# Revit family: Columns_&_Screens-Teknion-RCSLG_Lateral_Screen_for_Spine_Desk_Glass-R2019
name_source: partatom
category: Furniture
units: mm (PartAtom-declared; Revit-internal decimal feet)

## family parameters
Always vertical = Yes
Cut with Voids When Loaded = No
OmniClass Number = 23.40.20.00
OmniClass Title = General Furniture and Specialties
Room Calculation Point = No
Shared = Yes
Work Plane-Based = No

## types (9) — shared parameters
Assembly Code = E2020200
Bottom of Screen = 29 "
Manufacturer = Teknion
Manufacturer Fax = 416.661.4586
Part Number = RCSLG
Product Documentation Link = https://www.teknion.com
Product Line = Expansion Desking
Product Page URL = https://www.teknion.com
Series = Expansion Desking
Sustainability Data = https://www.teknion.com
URL = www.teknion.com
Unit Weight URL = http://www.teknion.com
Warranty = http://www.teknion.com

## per-type parameters (varying)
| type | Description | From Rear Edge | From Two Central Screens | From Two Mounted Storage | Height | Model | Screen Offset |
| From Two Central Screens, 51" High Datum Line With Desk-Mounted Option | Lateral Screen for Spine Desk - Glass, From Two Central Screens, 51" High Datum Line with Desk-Mounted option | No | Yes | No | 50.831 " | RCSLGC22__ | 0.508 " |
| From Two Central Screens, 42" High Datum Line With Desk-Mounted Option | Lateral Screen for Spine Desk - Glass, From Two Central Screens, 42" High Datum Line with Desk-Mounted option | No | Yes | No | 42 " | RCSLGC13__ | 0.508 " |
| From Two Central Screens, Desk-Mounted Shelf Height With Desk-Mounted Option | Lateral Screen for Spine Desk - Glass, From Two Central Screens, Desk-Mounted Shelf Height with Desk-Mounted option | No | Yes | No | 36.071 " | RCSLGC07__ | 0.508 " |
| From Rear Edge, 42" High Datum Line With Desk-Mounted Option | Lateral Screen for Spine Desk - Glass, From Rear Edge , 42" High Datum Line with Desk-Mounted option | Yes | No | No | 42 " | RCSLGE13__ | 0 " |
| From Two Mounted Storage, 42" High Datum Line With Desk-Mounted Option | Lateral Screen for Spine Desk - Glass, From Two Mounted Storage , 42" High Datum Line with Desk-Mounted option | No | No | Yes | 42 " | RCSLGM13__ | 0 " |
| From Rear Edge, 51" High Datum Line With Desk-Mounted Option | Lateral Screen for Spine Desk - Glass, From Rear Edge, 51" High Datum Line with Desk-Mounted option | Yes | No | No | 50.831 " | RCSLGE22__ | 0 " |
| From Two Mounted Storage, 51" High Datum Line With Desk-Mounted Option | Lateral Screen for Spine Desk - Glass, From Two Mounted Storage, 51" High Datum Line with Desk-Mounted option | No | No | Yes | 50.831 " | RCSLGM22__ | 0 " |
| From Rear Edge, Desk-Mounted Shelf Height With Desk-Mounted Option | Lateral Screen for Spine Desk - Glass, From Rear Edge, Desk-Mounted Shelf Height with Desk-Mounted option | Yes | No | No | 36.071 " | RCSLGE07__ | 0 " |
| From Two Mounted Storage, Desk-Mounted Shelf Height With Desk-Mounted Option | Lateral Screen for Spine Desk - Glass, From Two Mounted Storage, Desk-Mounted Shelf Height with Desk-Mounted option | No | No | Yes | 36.071 " | RCSLGM07__ | 0 " |

## geometry (parser evidence)
native form markers: Sweep x2
no freeform markers — native parametric forms only
